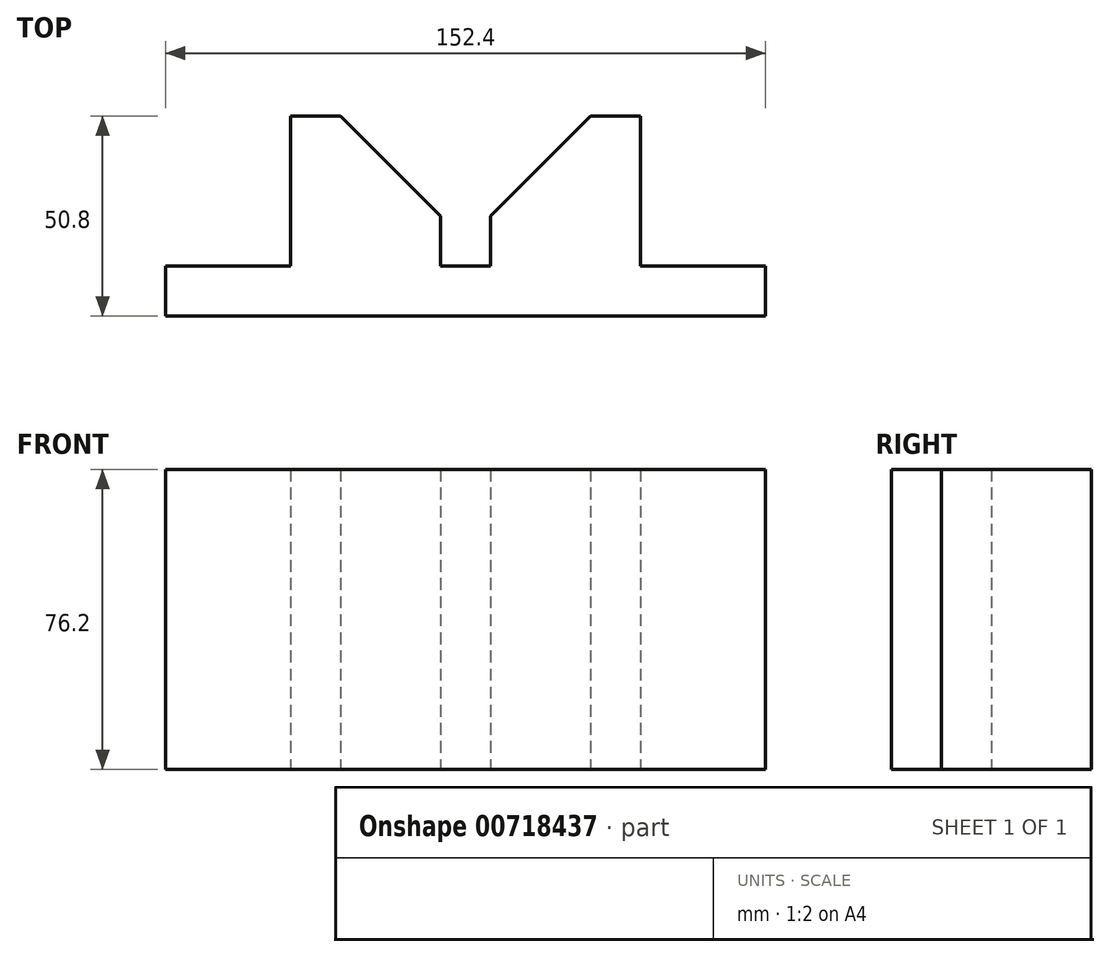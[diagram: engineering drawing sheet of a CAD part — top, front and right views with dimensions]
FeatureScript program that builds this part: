
annotation { "Feature Type Name" : "Feature", "Feature Type Description" : "" }
export const myFeature = defineFeature(function(context is Context, id is Id, definition is map)
    precondition{}
    {
        {
            var Q0;
            Q0=qCreatedBy(makeId("Top.planeOp"),FACE);
            var sketch = newSketch(context, id + "F0", { "sketchPlane" : qUnion([Q0])});
            skLineSegment(sketch, "E0", {"start": v(-70.96, 35.9) * mm, "end": v(-70.96, -2.2) * mm});
            skLineSegment(sketch, "E1", {"start": v(-70.96, -2.2) * mm, "end": v(-102.7, -2.2) * mm});
            skLineSegment(sketch, "E2", {"start": v(-102.7, -2.2) * mm, "end": v(-102.7, -14.9) * mm});
            skLineSegment(sketch, "E3", {"start": v(-102.7, -14.9) * mm, "end": v(49.7, -14.9) * mm});
            skLineSegment(sketch, "E4", {"start": v(49.7, -14.9) * mm, "end": v(49.7, -2.2) * mm});
            skLineSegment(sketch, "E5", {"start": v(49.7, -2.2) * mm, "end": v(17.94, -2.2) * mm});
            skLineSegment(sketch, "E6", {"start": v(17.94, -2.2) * mm, "end": v(17.94, 35.9) * mm});
            skLineSegment(sketch, "E7", {"start": v(-70.96, 35.9) * mm, "end": v(-58.26, 35.9) * mm});
            skLineSegment(sketch, "E8", {"start": v(5.24, 35.9) * mm, "end": v(17.94, 35.9) * mm});
            skLineSegment(sketch, "E9", {"start": v(-32.86, 10.5) * mm, "end": v(-32.86, -2.2) * mm});
            skLineSegment(sketch, "E10", {"start": v(-32.86, -2.2) * mm, "end": v(-20.16, -2.2) * mm});
            skLineSegment(sketch, "E11", {"start": v(-20.16, 10.5) * mm, "end": v(-20.16, -2.2) * mm});
            skLineSegment(sketch, "E12", {"start": v(-20.16, 10.5) * mm, "end": v(5.24, 35.9) * mm});
            skLineSegment(sketch, "E13", {"start": v(-32.86, 10.5) * mm, "end": v(-58.26, 35.9) * mm});
            skSolve(sketch);
        }
        {
            var Q0;
            Q0=qSketchRegion(id+"F0",true);
            extrude(context, id + "F1", {"entities" : qUnion([Q0]), "depth" : 76.2 * mm, "offsetDistance" : 25.4 * mm});
        }
    });
